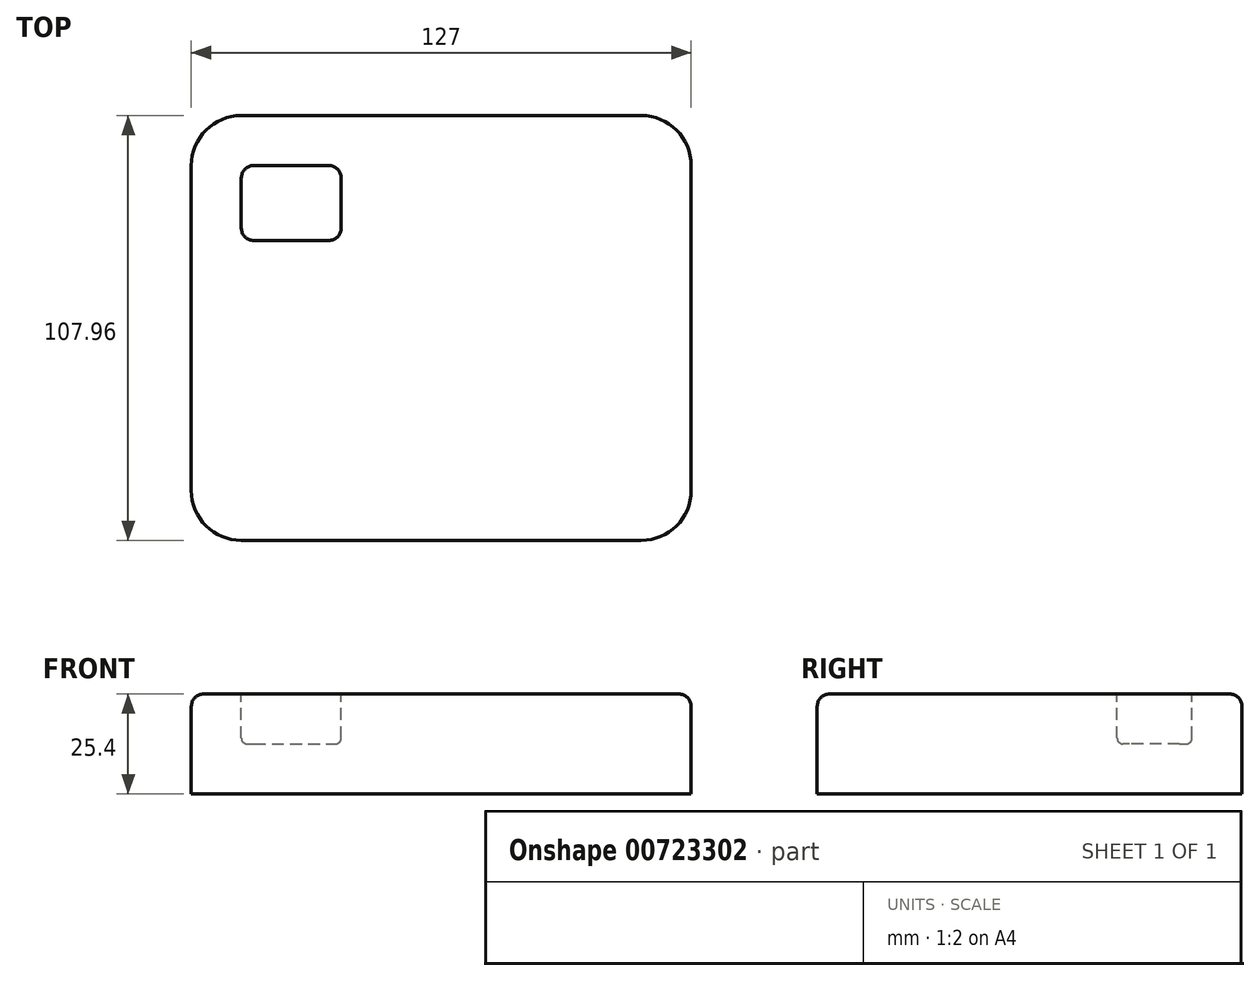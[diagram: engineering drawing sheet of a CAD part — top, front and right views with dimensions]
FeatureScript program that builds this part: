
annotation { "Feature Type Name" : "Feature", "Feature Type Description" : "" }
export const myFeature = defineFeature(function(context is Context, id is Id, definition is map)
    precondition{}
    {
        {
            var Q0;
            Q0=qCreatedBy(makeId("Top.planeOp"),FACE);
            var sketch = newSketch(context, id + "F0", { "sketchPlane" : qUnion([Q0])});
            skLineSegment(sketch, "E0.bottom", {"start": v(63.5, 53.98) * mm, "end": v(-63.5, 53.98) * mm});
            skLineSegment(sketch, "E0.top", {"start": v(63.5, -53.98) * mm, "end": v(-63.5, -53.98) * mm});
            skLineSegment(sketch, "E0.left", {"start": v(63.5, 53.98) * mm, "end": v(63.5, -53.98) * mm});
            skLineSegment(sketch, "E0.right", {"start": v(-63.5, 53.98) * mm, "end": v(-63.5, -53.98) * mm});
            skPoint(sketch, "E0.middle", {"position": v(0, 0) * mm});
            skSolve(sketch);
        }
        {
            var Q0;
            Q0=makeQuery(id+"F0.imprint","IMPRINT",FACE,{"disambiguationData":[TD([[makeQuery(id+"F0.imprint","IMPRINT",EDGE,{"derivedFrom":sQuery(id+"F0.wireOp",EDGE,"E0.bottom")}),1.0]])]});
            extrude(context, id + "F1", {"entities" : qUnion([Q0]), "depth" : 25.4 * mm});
        }
        {
            var Q0;
            Q0=makeQuery(id+"F1.opExtrude","CAP_FACE",FACE,{"disambiguationData":[OSD([sQuery(id+"F0.wireOp",EDGE,"E0.bottom"),sQuery(id+"F0.wireOp",EDGE,"E0.top"),sQuery(id+"F0.wireOp",EDGE,"E0.left"),sQuery(id+"F0.wireOp",EDGE,"E0.right")])],"isStart":false});
            var sketch = newSketch(context, id + "F2", { "sketchPlane" : qUnion([Q0])});
            skLineSegment(sketch, "E1.bottom", {"start": v(-50.8, 41.28) * mm, "end": v(-25.4, 41.28) * mm});
            skLineSegment(sketch, "E1.top", {"start": v(-50.8, 22.23) * mm, "end": v(-25.4, 22.23) * mm});
            skLineSegment(sketch, "E1.left", {"start": v(-50.8, 41.28) * mm, "end": v(-50.8, 22.23) * mm});
            skLineSegment(sketch, "E1.right", {"start": v(-25.4, 41.28) * mm, "end": v(-25.4, 22.23) * mm});
            skSolve(sketch);
        }
        {
            var Q0;
            Q0=makeQuery(id+"F2.imprint","IMPRINT",FACE,{"disambiguationData":[TD([[makeQuery(id+"F2.imprint","IMPRINT",EDGE,{"derivedFrom":sQuery(id+"F2.wireOp",EDGE,"E1.bottom")}),-1.0]])]});
            extrude(context, id + "F3", {"entities" : qUnion([Q0]), "operationType" : NewBodyOperationType.REMOVE, "oppositeDirection" : true, "depth" : 12.7 * mm});
        }
        {
            var Q0;
            Q0=makeQuery(id+"F3.boolean.opBoolean","COPY",EDGE,{"derivedFrom":makeQuery(id+"F3.opExtrude","SWEPT_EDGE",EDGE,{"disambiguationData":[OSD([sQuery(id+"F2.wireOp",EDGE,"E1.bottom"),sQuery(id+"F2.wireOp",EDGE,"E1.left")])]})});
            var Q1;
            Q1=makeQuery(id+"F3.boolean.opBoolean","COPY",EDGE,{"derivedFrom":makeQuery(id+"F3.opExtrude","SWEPT_EDGE",EDGE,{"disambiguationData":[OSD([sQuery(id+"F2.wireOp",EDGE,"E1.top"),sQuery(id+"F2.wireOp",EDGE,"E1.left")])]})});
            var Q2;
            Q2=makeQuery(id+"F3.boolean.opBoolean","COPY",EDGE,{"derivedFrom":makeQuery(id+"F3.opExtrude","SWEPT_EDGE",EDGE,{"disambiguationData":[OSD([sQuery(id+"F2.wireOp",EDGE,"E1.top"),sQuery(id+"F2.wireOp",EDGE,"E1.right")])]})});
            var Q3;
            Q3=makeQuery(id+"F3.boolean.opBoolean","COPY",EDGE,{"derivedFrom":makeQuery(id+"F3.opExtrude","SWEPT_EDGE",EDGE,{"disambiguationData":[OSD([sQuery(id+"F2.wireOp",EDGE,"E1.bottom"),sQuery(id+"F2.wireOp",EDGE,"E1.right")])]})});
            fillet(context, id + "F4", {"entities" : qUnion([Q0, Q1, Q2, Q3]), "radius" : 3.17 * mm, "tangentPropagation" : true, "allowEdgeOverflow" : false});
        }
        {
            var Q0;
            Q0=makeQuery(id+"F3.boolean.opBoolean","COPY",EDGE,{"derivedFrom":makeQuery(id+"F3.opExtrude","CAP_EDGE",EDGE,{"disambiguationData":[OSD([sQuery(id+"F2.wireOp",EDGE,"E1.top")])],"isStart":false})});
            fillet(context, id + "F5", {"entities" : qUnion([Q0]), "radius" : 1.52 * mm, "tangentPropagation" : true, "allowEdgeOverflow" : false});
        }
        {
            var Q0;
            Q0=makeQuery(id+"F1.opExtrude","SWEPT_EDGE",EDGE,{"disambiguationData":[OSD([sQuery(id+"F0.wireOp",EDGE,"E0.top"),sQuery(id+"F0.wireOp",EDGE,"E0.left")])]});
            var Q1;
            Q1=makeQuery(id+"F1.opExtrude","SWEPT_EDGE",EDGE,{"disambiguationData":[OSD([sQuery(id+"F0.wireOp",EDGE,"E0.bottom"),sQuery(id+"F0.wireOp",EDGE,"E0.left")])]});
            var Q2;
            Q2=makeQuery(id+"F1.opExtrude","SWEPT_EDGE",EDGE,{"disambiguationData":[OSD([sQuery(id+"F0.wireOp",EDGE,"E0.top"),sQuery(id+"F0.wireOp",EDGE,"E0.right")])]});
            var Q3;
            Q3=makeQuery(id+"F1.opExtrude","SWEPT_EDGE",EDGE,{"disambiguationData":[OSD([sQuery(id+"F0.wireOp",EDGE,"E0.bottom"),sQuery(id+"F0.wireOp",EDGE,"E0.right")])]});
            fillet(context, id + "F6", {"entities" : qUnion([Q0, Q1, Q2, Q3]), "radius" : 12.7 * mm, "tangentPropagation" : true, "allowEdgeOverflow" : false});
        }
        {
            var Q0;
            Q0=makeQuery(id+"F1.opExtrude","CAP_EDGE",EDGE,{"disambiguationData":[OSD([sQuery(id+"F0.wireOp",EDGE,"E0.top")])],"isStart":false});
            fillet(context, id + "F7", {"entities" : qUnion([Q0]), "radius" : 3.17 * mm, "tangentPropagation" : true, "allowEdgeOverflow" : false});
        }
    });
